# Revit family: DPRV_DN025_RFA_2018
name_source: partatom
category: Pipe Accessories
revit_build: Autodesk Revit LT 2018 (Build: 20180329_1100(x64)
units: mm (PartAtom-declared; Revit-internal decimal feet)

## family parameters
Always vertical = Yes
Cut with Voids When Loaded = No
Part Type = Valve - Breaks Into
Round Connector Dimension = Use Diameter
Shared = No
Work Plane-Based = No

## types (4) — shared parameters
Description = Nastavitelný přepouštěcí ventil
H5 = 3 mm  [stored 0.00984252 ft]
L2D = 70 mm
L2D_Min = 30 mm  [stored 0.0984252 ft]
MC Pressure Drop Maximum Value = 0.0 Pa
MC Pressure Drop Minimum Value = 0.0 Pa
MC Use Limits From Balancing Method = No
Manufacturer = Hydronix
QmdConnectorList = 301;D;302;D
Type Comments = závitový s vnitřním závitem; PN25; dpmax=600kPa; -20~+120°C
URL = www.hydronix.cz
W2D = 15 mm  [stored 0.0492126 ft]
XT0 = 8 mm  [stored 0.0262467 ft]
magiPartTypeId = 304
magiProductFamilyId = 2368235d042246b783f613dde97580
zero-valued in all types: MC Throttling Maximum Value, MC Throttling Minimum Value

## per-type parameters (varying)
- DPRV-DN15: AA2=5 mm  [stored 0.0164042 ft]; AA3=3 mm  [stored 0.00984252 ft]; CenSd_L3_6=13 mm; CenSd_Y14_6=11 mm  [stored 0.0360892 ft]; D=15 mm; DT2=8 mm  [stored 0.0262467 ft]; H2=22 mm; H6=31 mm; L3=15 mm  [stored 0.0492126 ft]; MC Product Code=48-0075; DN15 FF; nastavitelný rozsah 10-60kPa; kvs=3,5; X0=35 mm  [stored 0.114829 ft]; X1=7 mm  [stored 0.0229659 ft]; X1__ve=-7 mm  [stored -0.0229659 ft]; X3=2 mm  [stored 0.00656168 ft]; X6=13 mm; X6__ve=-13 mm; X7=5 mm  [stored 0.0164042 ft]; Y0=10 mm  [stored 0.0328084 ft]; Y10=11 mm  [stored 0.0360892 ft]; Y11=12 mm  [stored 0.0393701 ft]; Y12=9 mm  [stored 0.0295276 ft]; Y14=13 mm; Y15=11 mm  [stored 0.0360892 ft]; Y3=12 mm  [stored 0.0393701 ft]; Y5=11 mm  [stored 0.0360892 ft]; Y6=13 mm; Z1=26 mm; magiProductId=0a1695ce379549c5bda4e9817c8a32
- DPRV-DN20: AA2=5 mm  [stored 0.0164042 ft]; AA3=3 mm  [stored 0.00984252 ft]; CenSd_L3_6=16 mm  [stored 0.0524934 ft]; CenSd_Y14_6=12 mm  [stored 0.0393701 ft]; D=20 mm; DT2=10 mm  [stored 0.0328084 ft]; H2=22 mm; H6=31 mm; L3=18 mm  [stored 0.0590551 ft]; MC Product Code=48-0076; DN20 FF; nastavitelný rozsah 10-60kPa; kvs=3,7; X0=39 mm  [stored 0.127953 ft]; X1=8 mm  [stored 0.0262467 ft]; X1__ve=-8 mm  [stored -0.0262467 ft]; X3=2 mm  [stored 0.00656168 ft]; X6=14 mm  [stored 0.0459318 ft]; X6__ve=-14 mm; X7=5 mm  [stored 0.0164042 ft]; Y0=12 mm  [stored 0.0393701 ft]; Y10=12 mm  [stored 0.0393701 ft]; Y11=13 mm; Y12=10 mm  [stored 0.0328084 ft]; Y14=14 mm  [stored 0.0459318 ft]; Y15=12 mm  [stored 0.0393701 ft]; Y3=14 mm  [stored 0.0459318 ft]; Y5=13 mm; Y6=15 mm  [stored 0.0492126 ft]; Z1=26 mm; magiProductId=7bf90d6895024d90850a4e7c13d0c4
- DPRV-DN25: AA2=7 mm  [stored 0.0229659 ft]; AA3=4 mm  [stored 0.0131234 ft]; CenSd_L3_6=20 mm  [stored 0.0656168 ft]; CenSd_Y14_6=14 mm  [stored 0.0459318 ft]; D=25 mm; DT2=13 mm; H2=24 mm; H6=33 mm; L3=23 mm  [stored 0.0754593 ft]; MC Product Code=48-0077; DN25 FF; nastavitelný rozsah 10-60kPa; kvs=8,3; X0=44 mm; X1=9 mm  [stored 0.0295276 ft]; X1__ve=-9 mm; X3=3 mm  [stored 0.00984252 ft]; X6=16 mm  [stored 0.0524934 ft]; X6__ve=-16 mm; X7=6 mm  [stored 0.019685 ft]; Y0=16 mm  [stored 0.0524934 ft]; Y10=14 mm  [stored 0.0459318 ft]; Y11=15 mm  [stored 0.0492126 ft]; Y12=11 mm  [stored 0.0360892 ft]; Y14=16 mm  [stored 0.0524934 ft]; Y15=13 mm; Y3=18 mm  [stored 0.0590551 ft]; Y5=17 mm; Y6=20 mm  [stored 0.0656168 ft]; Z1=28 mm  [stored 0.0918635 ft]; magiProductId=8f5d2c47d0804d84a9ee1a0f7163ce
- DPRV-DN32: AA2=7 mm  [stored 0.0229659 ft]; AA3=4 mm  [stored 0.0131234 ft]; CenSd_L3_6=24 mm; CenSd_Y14_6=16 mm  [stored 0.0524934 ft]; D=32 mm; DT2=16 mm  [stored 0.0524934 ft]; H2=24 mm; H6=33 mm; L3=28 mm  [stored 0.0918635 ft]; MC Product Code=48-0078; DN32 FF; nastavitelný rozsah 10-60kPa; kvs=10,5; X0=52 mm; X1=10 mm  [stored 0.0328084 ft]; X1__ve=-10 mm  [stored -0.0328084 ft]; X3=3 mm  [stored 0.00984252 ft]; X6=19 mm; X6__ve=-19 mm; X7=7 mm  [stored 0.0229659 ft]; Y0=19 mm; Y10=16 mm  [stored 0.0524934 ft]; Y11=18 mm  [stored 0.0590551 ft]; Y12=13 mm; Y14=19 mm; Y15=16 mm  [stored 0.0524934 ft]; Y3=22 mm; Y5=21 mm; Y6=24 mm; Z1=28 mm  [stored 0.0918635 ft]; magiProductId=4b273c145a0a4466be66f0b82dd13f

note: [stored X ft] marks values corroborated as IEEE doubles in the binary element streams (Revit-internal decimal feet)

## geometry (parser evidence)
native form markers: Sweep x1
no freeform markers — native parametric forms only
